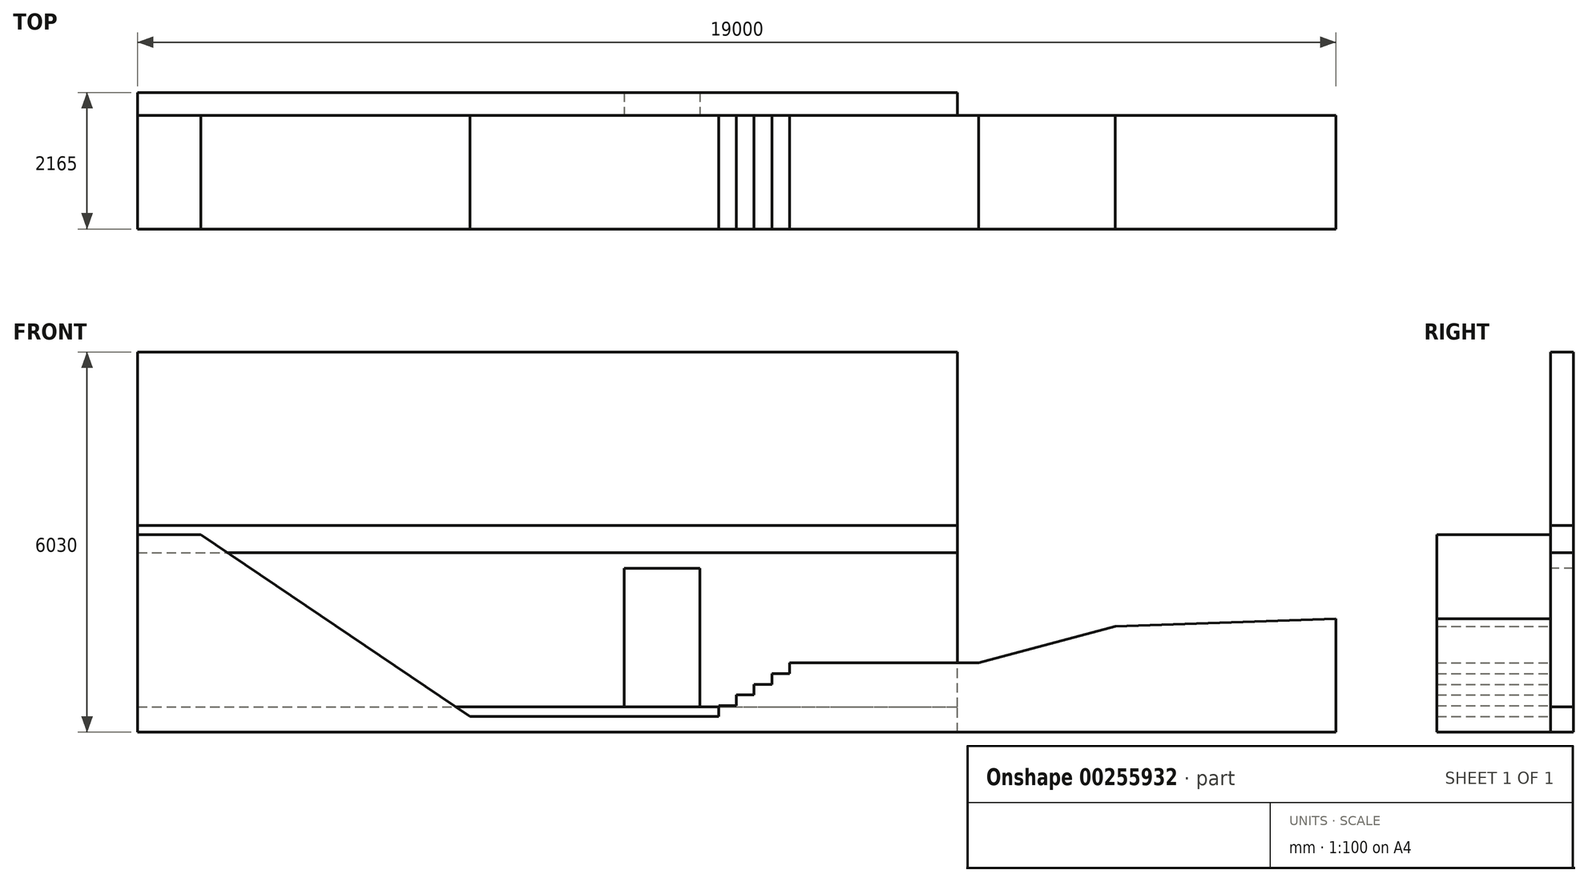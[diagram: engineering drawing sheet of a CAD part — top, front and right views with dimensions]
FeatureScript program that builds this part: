
annotation { "Feature Type Name" : "Feature", "Feature Type Description" : "" }
export const myFeature = defineFeature(function(context is Context, id is Id, definition is map)
    precondition{}
    {
        {
            var Q0;
            Q0=qCreatedBy(makeId("Front.planeOp"),FACE);
            var sketch = newSketch(context, id + "F0", { "sketchPlane" : qUnion([Q0])});
            skLineSegment(sketch, "E0.bottom", {"start": v(0, 0) * mm, "end": v(13000, 0) * mm});
            skLineSegment(sketch, "E0.top", {"start": v(0, 400) * mm, "end": v(13000, 400) * mm});
            skLineSegment(sketch, "E0.left", {"start": v(0, 0) * mm, "end": v(0, 400) * mm});
            skLineSegment(sketch, "E0.right", {"start": v(13000, 0) * mm, "end": v(13000, 400) * mm});
            skSolve(sketch);
        }
        {
            var Q0;
            Q0=qSketchRegion(id+"F0",true);
            extrude(context, id + "F1", {"entities" : qUnion([Q0]), "depth" : 365 * mm});
        }
        {
            var Q0;
            Q0=makeQuery(id+"F1.opExtrude","CAP_FACE",FACE,{"disambiguationData":[OSD([sQuery(id+"F0.wireOp",EDGE,"E0.bottom"),sQuery(id+"F0.wireOp",EDGE,"E0.top"),sQuery(id+"F0.wireOp",EDGE,"E0.left"),sQuery(id+"F0.wireOp",EDGE,"E0.right")])],"isStart":false});
            var sketch = newSketch(context, id + "F2", { "sketchPlane" : qUnion([Q0])});
            skLineSegment(sketch, "E1.bottom", {"start": v(0, 400) * mm, "end": v(7715, 400) * mm});
            skLineSegment(sketch, "E1.top", {"start": v(0, 2850) * mm, "end": v(13000, 2850) * mm});
            skLineSegment(sketch, "E1.left", {"start": v(0, 400) * mm, "end": v(0, 2850) * mm});
            skLineSegment(sketch, "E1.right", {"start": v(13000, 400) * mm, "end": v(13000, 2850) * mm});
            skLineSegment(sketch, "E2", {"start": v(8915, 400) * mm, "end": v(8915, 2600) * mm});
            skLineSegment(sketch, "E3", {"start": v(8915, 2600) * mm, "end": v(7715, 2600) * mm});
            skLineSegment(sketch, "E4", {"start": v(7715, 2600) * mm, "end": v(7715, 400) * mm});
            skLineSegment(sketch, "E5.trimOffspring", {"start": v(8915, 400) * mm, "end": v(13000, 400) * mm});
            skSolve(sketch);
        }
        {
            var Q0;
            Q0=qSketchRegion(id+"F2",true);
            extrude(context, id + "F3", {"entities" : qUnion([Q0]), "oppositeDirection" : true, "depth" : 365 * mm});
        }
        {
            var Q0;
            Q0=qCreatedBy(makeId("Front.planeOp"),FACE);
            var sketch = newSketch(context, id + "F4", { "sketchPlane" : qUnion([Q0])});
            skLineSegment(sketch, "E6.bottom", {"start": v(0, 2850) * mm, "end": v(13000, 2850) * mm});
            skLineSegment(sketch, "E6.top", {"start": v(0, 3280) * mm, "end": v(13000, 3280) * mm});
            skLineSegment(sketch, "E6.left", {"start": v(0, 2850) * mm, "end": v(0, 3280) * mm});
            skLineSegment(sketch, "E6.right", {"start": v(13000, 2850) * mm, "end": v(13000, 3280) * mm});
            skSolve(sketch);
        }
        {
            var Q0;
            Q0=qSketchRegion(id+"F4",true);
            extrude(context, id + "F5", {"entities" : qUnion([Q0]), "depth" : 365 * mm});
        }
        {
            var Q0;
            Q0=qCreatedBy(makeId("Front.planeOp"),FACE);
            var sketch = newSketch(context, id + "F6", { "sketchPlane" : qUnion([Q0])});
            skLineSegment(sketch, "E7.bottom", {"start": v(0, 3280) * mm, "end": v(13000, 3280) * mm});
            skLineSegment(sketch, "E7.top", {"start": v(0, 6030) * mm, "end": v(13000, 6030) * mm});
            skLineSegment(sketch, "E7.left", {"start": v(0, 3280) * mm, "end": v(0, 6030) * mm});
            skLineSegment(sketch, "E7.right", {"start": v(13000, 3280) * mm, "end": v(13000, 6030) * mm});
            skSolve(sketch);
        }
        {
            var Q0;
            Q0=qSketchRegion(id+"F6",true);
            extrude(context, id + "F7", {"entities" : qUnion([Q0]), "depth" : 365 * mm});
        }
        {
            var Q0;
            Q0=makeQuery(id+"F3.opExtrude","CAP_FACE",FACE,{"disambiguationData":[OSD([sQuery(id+"F2.wireOp",EDGE,"E1.bottom"),sQuery(id+"F2.wireOp",EDGE,"E1.top"),sQuery(id+"F2.wireOp",EDGE,"E1.left"),sQuery(id+"F2.wireOp",EDGE,"E1.right"),sQuery(id+"F2.wireOp",EDGE,"E2"),sQuery(id+"F2.wireOp",EDGE,"E3"),sQuery(id+"F2.wireOp",EDGE,"E4"),sQuery(id+"F2.wireOp",EDGE,"E5.trimOffspring")])],"isStart":true});
            var sketch = newSketch(context, id + "F8", { "sketchPlane" : qUnion([Q0])});
            skLineSegment(sketch, "E8", {"start": v(-1000, 3200) * mm, "end": v(19000, 1800) * mm});
            skLineSegment(sketch, "E9", {"start": v(19000, 1800) * mm, "end": v(19000, 0) * mm});
            skLineSegment(sketch, "E10", {"start": v(19000, 0) * mm, "end": v(-1000, 0) * mm});
            skLineSegment(sketch, "E11", {"start": v(-1000, 3200) * mm, "end": v(-1000, 0) * mm});
            skPoint(sketch, "E12", {"position": v(0, 3130) * mm});
            skSolve(sketch);
        }
        {
            var Q0;
            Q0=makeQuery(id+"F3.opExtrude","CAP_FACE",FACE,{"disambiguationData":[OSD([sQuery(id+"F2.wireOp",EDGE,"E1.bottom"),sQuery(id+"F2.wireOp",EDGE,"E1.top"),sQuery(id+"F2.wireOp",EDGE,"E1.left"),sQuery(id+"F2.wireOp",EDGE,"E1.right"),sQuery(id+"F2.wireOp",EDGE,"E2"),sQuery(id+"F2.wireOp",EDGE,"E3"),sQuery(id+"F2.wireOp",EDGE,"E4"),sQuery(id+"F2.wireOp",EDGE,"E5.trimOffspring")])],"isStart":true});
            var sketch = newSketch(context, id + "F9", { "sketchPlane" : qUnion([Q0])});
            skLineSegment(sketch, "E13", {"start": v(0, 3130) * mm, "end": v(1000, 3130) * mm});
            skLineSegment(sketch, "E14", {"start": v(1000, 3130) * mm, "end": v(5269.78, 250) * mm});
            skLineSegment(sketch, "E15", {"start": v(5269.78, 250) * mm, "end": v(9215, 250) * mm});
            skLineSegment(sketch, "E16", {"start": v(15500, 1677.78) * mm, "end": v(19000, 1800) * mm});
            skLineSegment(sketch, "E17", {"start": v(19000, 1800) * mm, "end": v(19000, 0) * mm});
            skLineSegment(sketch, "E18", {"start": v(19000, 0) * mm, "end": v(0, 0) * mm});
            skLineSegment(sketch, "E19", {"start": v(0, 0) * mm, "end": v(0, 3130) * mm});
            skLineSegment(sketch, "E20", {"start": v(9215, 250) * mm, "end": v(9215, 420) * mm});
            skLineSegment(sketch, "E21", {"start": v(9215, 420) * mm, "end": v(9495, 420) * mm});
            skLineSegment(sketch, "E22", {"start": v(9495, 420) * mm, "end": v(9495, 590) * mm});
            skLineSegment(sketch, "E23", {"start": v(9495, 590) * mm, "end": v(9775, 590) * mm});
            skLineSegment(sketch, "E24", {"start": v(9775, 590) * mm, "end": v(9775, 760) * mm});
            skLineSegment(sketch, "E25", {"start": v(9775, 760) * mm, "end": v(10055, 760) * mm});
            skLineSegment(sketch, "E26", {"start": v(10055, 760) * mm, "end": v(10055, 930) * mm});
            skLineSegment(sketch, "E27", {"start": v(10055, 930) * mm, "end": v(10335, 930) * mm});
            skLineSegment(sketch, "E28", {"start": v(10335, 930) * mm, "end": v(10335, 1100) * mm});
            skLineSegment(sketch, "E29", {"start": v(10335, 1100) * mm, "end": v(13335, 1100) * mm});
            skLineSegment(sketch, "E30", {"start": v(13335, 1100) * mm, "end": v(15500, 1677.78) * mm});
            skSolve(sketch);
        }
        {
            var Q0;
            Q0=qSketchRegion(id+"F9",true);
            extrude(context, id + "F10", {"entities" : qUnion([Q0]), "depth" : 1800 * mm});
        }
    });
